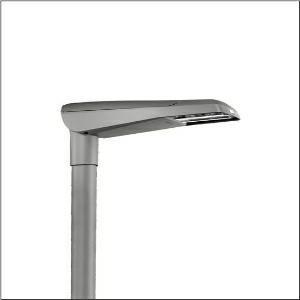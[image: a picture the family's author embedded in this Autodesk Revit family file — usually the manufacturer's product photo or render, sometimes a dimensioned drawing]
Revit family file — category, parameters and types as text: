
# Revit family: streetlight_sl_11_iq_micro___st1_0ab_5xc1nc1f08de_8c0d
name_source: partatom
category: Lighting Fixtures
units: mm (PartAtom-declared; Revit-internal decimal feet)

## family parameters
Cut with Voids When Loaded = No
Host = Face
Light Source = No
Part Type = Normal
Room Calculation Point = No
Round Connector Dimension = Use Diameter
Shared = No

## types (1)
- --- (1 x LED, 3090 lm, 27.4 W, 4000K)
    Apparent Load = 27 VA
    CIE Flux Codes = 29 63 95 100 100
    Color Rendering = 70
    Color Temperature = 4000K
    Default Elevation = 1800 mm
    Description = Streetlight SL 11 iQ micro, mast luminaire, primary light control with 3 zone facetted reflector, of plastic, silver coated, highly specular, primary optical cover: cover, of PMMA, transparent, light distribution: ST1.0aB, light emission: direct distribution, primary light characteristic: asymmetric, installation type: post-top, side-entry, LED, High Power LED, rated luminous flux: 3.050lm, luminous efficacy: 110lm/W, light colour: 722/727/730/740, colour temperature: 2200/2700/3000/4000K, control gear: iQ Street-Remote, control: Street-Remote, Auto-Match, Temp-Guard, Lumen-Switch, Night-Set, Smart-Wire, Light-Fading, Desk-Remote (wireless, voltage-free reading and setting of iQ features in the workshop via application-optimized NFC function/RFID function), optimised constant luminous flux control (CLO 2.0), with cable H07RN-F 5x 1.5mm², mains connection: 220..240V, AC, 50/60Hz, connection cable pre-assembled, cable length: 6,5m, start of lifetime: 28W, end of service life: 28W, reduction: 13W, luminaire housing, of diecast aluminium, powder-coated, Siteco® metallic grey (DB 702S), please order mast flange separately, inclination adjustable without tools: 0°, 5°, 10°, 15° (post-top) | 0°, -5°, -10°, -15° (side-entry), sealing non-destructively replaceable, multi-level sealing system, length: 600mm, width: 174mm, height: 116mm, mast flange for spigot size: 42mm (side-entry): 5XC10008XM4, 60/48mm (side-entry/post-top): 5XC10108XM2, 76/60mm (side-entry/post-top): 5XC10108XM1, mounting height: 4..8m, equipment: Power, protection rating (complete): IP66, insulation class (complete): insulation class II (safety insulation), certification: CE, ENEC, VDE, impact resistance: IK09, permissible operating ambient temperature for outdoor applications: -25..+50°C, standard-compliant lighting for roads and squares, Environmental Product Declaration (EPD) tested and certified by an independent institute, packaging unit: 1 piece

Light Distribution: ST1.0aB
    Height = 116 mm
    Lamp = 1 x LED
    Lamp Light Flux = 3090 lm
    Lamp Power = 27.4 W
    Lamp count = 1
    Length = 600 mm
    Luminous efficacy = 113 lm/W
    Manufacturer = Siteco
    ModVariant = No
    Model = 5XC1NC1F08DE
    Number of Poles = 1
    OnlyDefault = Yes
    Power Factor = 1
    Product Name = Streetlight SL 11 iQ micro | ST1.0aB
    Product group = mast luminaire | pylon top
    ProductGroupID = 6100
    Protection Class = Protection class II
    Protection Degree = IP 66
    RLX_Detail_Level = 1
    RLX_Emergency_Light_Flux = 0 lm
    RLX_Emergency_Type = 0
    RLX_Emergency_Type_DB = No
    RlxData = <blob elided: 35469 chars, md5=6683a572>
    Socket = socket
    Standby Power = 0 W
    System Light Flux = 3090 lm
    System Power = 27 W
    Type Comments = individual setting: luminous flux: 100 % | dim-lin: 254 | 726 mA
    Type Image = l_1006566.jpg
    URL = http://relux.com
    VarID = @adj_001567
    Voltage = 0 V
    Weight = 0.00 kg
    Width = 174 mm

## geometry (parser evidence)
native form markers: Blend x4, Sweep x10
no freeform markers — native parametric forms only
